# Revit family: Druckminderer mit Kunststoffkappe 2682
name_source: partatom
category: Rohrzubehör
units: mm (PartAtom-declared; Revit-internal decimal feet)

## family parameters
Arbeitsebenenbasiert = Nein
Beim Laden mit Abzugskörper schneiden = Nein
Bemaßung runder Anschluss = Durchmesser verwenden
Gemeinsam genutzt = Nein
Immer vertikal = Ja
OmniClass-Nummer = 23.65.55.14
OmniClass-Titel = Valves for Liquid Services
Teiletyp = Unterbricht

## types (2) — shared parameters
Anwendung = Typischerweise dient der Druckreduzierer dazu, Installationen beziehungsweise Anlagen vor zu hohem Druck zu schützen.
Weiters können Druckreduzierer in Heizungsanlagen eingesetzt werden, um zu hohe Drücke im Boiler zu verhindern.
Der Druck nach dem Druckreduzierer ist im angegebenen Bereich einstellbar und steht nicht im Zusammenhang mit dem Vordruck.
Um den Druck nach dem Druckreduzierer zu steigern, muss der Handgriff im Uhrzeigersinn gedreht werden.
Durch das Einstellen von Drücken, welche die vorgegebene Skala überschreiten, können Schäden am Druckreduzierer entstehen.
Wir empfehlen einen maximalen Hinterdruck sekundärseitig von 4 bar für Anlagen in privaten Haushalten (lange Produktlebensdauer, geringe Kosten).
Nach jeder Änderung des Einstellwertes muss die Ausgangsseite druckentlastet werden, zum Beispiel durch Wasserzapfen.
Außengewinde = gemäß ISO 7-1 und ISO228
B02 = 26 mm  [stored 0.0853018 ft]
B03 = 5 mm  [stored 0.0164042 ft]
Dichtung der Holländeranschlüsse = Klingersil C-4324
Dichtung im Druckreduziererelement = EPDM
Einstellbereich (sekundärseitig) = 1.5 - 6 bar
Feder = Federstahl
Federführung = Edelstahl
Filter = Edelstahl
Gehäuse (DN15-DN25) = geschmiedetes Messing (EN 12165; CW626N)
Gehäuse (DN32-DN50) = Gussmessing (EN 1982; CC770S)
Handgriff = PA 6.6, grün
Hersteller = HERZ Armaturen Ges.m.b.H.
Hinweis = Gemäß Art 33 der REACH-Verordnung (EG Nr. 1907/2006) sind wir verpflichtet, darauf hinzuweisen, dass der Stoff Blei auf der SVHC-Liste geführt wird und dass alle aus Messing bestehenden Bauteile, die in unseren Erzeugnissen verarbeitet sind, mehr als 0,1 % (w/w) Blei (CAS: 7439-92-1 / EINECS: 231-100-4) enthalten.
Da Blei als Legierungsbestandteil fest gebunden ist, sind keine Expositionen zu erwarten und daher sind keine zusätzlichen Angaben zur sicheren Verwendung notwendig.
Holländeranschlüsse = Messing CW617N
Kappe = PA12, transparent
Manometeranschluss (beidseitig) = 1/4" F (ISO 228-1)
Manometerskala = 0 - 10 bar
Maschenweite Filter = 0.3 mm
Max. Betriebstemperatur = 40 °C
Max. Vordruck (primärseitig) = 1600000.0 Pa
Medium = Wasser
Membrane = EPDM
Oberteile = PA6.6
R06 = 19.5 mm  [stored 0.0639764 ft]
S02 = 10 mm  [stored 0.0328084 ft]
SCTWCODE = 04;24;02
SCTWSEQ = AW;SBT_TYP_AW="111";2
Standard = EN 1567
URL = www.herz-armaturen.at
W01 = 91.00°
Werkseinstellung (sekundärseitig) = 300000.0 Pa
zero-valued in all types: SC_NennweiteBerechnet

## type names (no varying parameters)
- Manometer vorne
- Manometer hinten

note: [stored X ft] marks values corroborated as IEEE doubles in the binary element streams (Revit-internal decimal feet)
